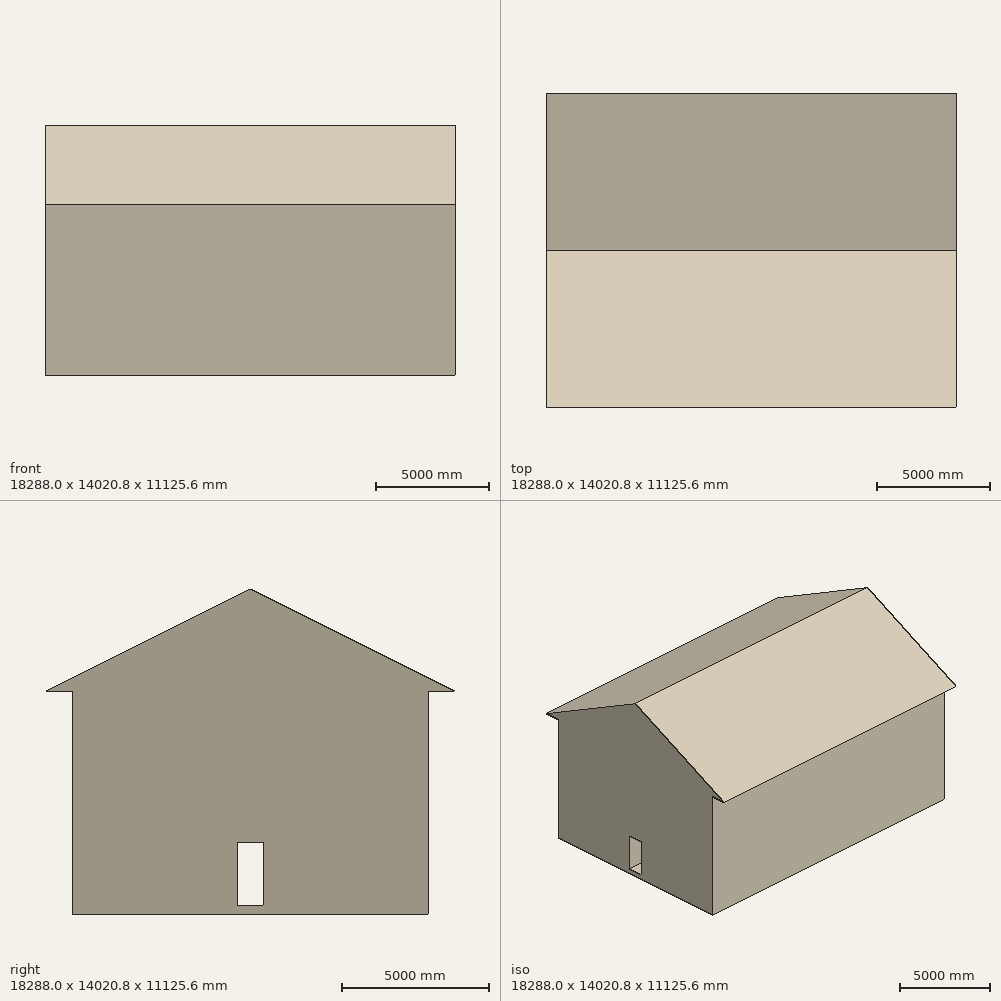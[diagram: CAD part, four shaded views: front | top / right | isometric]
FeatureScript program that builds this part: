
annotation { "Feature Type Name" : "Feature", "Feature Type Description" : "" }
export const myFeature = defineFeature(function(context is Context, id is Id, definition is map)
    precondition{}
    {
        {
            var Q0;
            Q0=qCreatedBy(makeId("Right.planeOp"),FACE);
            var sketch = newSketch(context, id + "F0", { "sketchPlane" : qUnion([Q0])});
            skLineSegment(sketch, "E0", {"start": v(0, 0) * mm, "end": v(-6096, 0) * mm});
            skLineSegment(sketch, "E1", {"start": v(-6096, 0) * mm, "end": v(-12192, 0) * mm});
            skLineSegment(sketch, "E2", {"start": v(-6096, 0) * mm, "end": v(-6096, 3048) * mm});
            skLineSegment(sketch, "E3", {"start": v(-12192, 0) * mm, "end": v(-6096, 3048) * mm});
            skLineSegment(sketch, "E4", {"start": v(0, 0) * mm, "end": v(-6096, 3048) * mm});
            skLineSegment(sketch, "E5", {"start": v(-12192, 0) * mm, "end": v(-12192, -7315.2) * mm});
            skLineSegment(sketch, "E6", {"start": v(-12192, -7315.2) * mm, "end": v(0, -7315.2) * mm});
            skLineSegment(sketch, "E7", {"start": v(0, 0) * mm, "end": v(0, -7315.2) * mm});
            skLineSegment(sketch, "E8", {"start": v(-12192, -7315.2) * mm, "end": v(-12192, -7620) * mm});
            skLineSegment(sketch, "E9", {"start": v(0, -7315.2) * mm, "end": v(0, -7620) * mm});
            skLineSegment(sketch, "E10", {"start": v(-12192, -7620) * mm, "end": v(0, -7620) * mm});
            skLineSegment(sketch, "E11", {"start": v(-6096, -7315.2) * mm, "end": v(-6553.2, -7315.2) * mm});
            skLineSegment(sketch, "E12", {"start": v(-6553.2, -7315.2) * mm, "end": v(-6553.2, -5181.6) * mm});
            skLineSegment(sketch, "E13", {"start": v(-6553.2, -5181.6) * mm, "end": v(-5638.8, -5181.6) * mm});
            skLineSegment(sketch, "E14", {"start": v(-5638.8, -5181.6) * mm, "end": v(-5638.8, -7315.2) * mm});
            skLineSegment(sketch, "E15", {"start": v(0, 0) * mm, "end": v(914.4, 0) * mm});
            skLineSegment(sketch, "E16", {"start": v(-12192, 0) * mm, "end": v(-13106.4, 0) * mm});
            skLineSegment(sketch, "E17", {"start": v(-13106.4, 0) * mm, "end": v(-6095.25, 3505.58) * mm});
            skLineSegment(sketch, "E18", {"start": v(-6095.25, 3505.58) * mm, "end": v(-6096, 3048) * mm});
            skLineSegment(sketch, "E19", {"start": v(-6095.25, 3505.58) * mm, "end": v(914.4, 0) * mm});
            skLineSegment(sketch, "E20.bottom", {"start": v(-10668, -914.4) * mm, "end": v(-9169.03, -914.4) * mm});
            skLineSegment(sketch, "E20.top", {"start": v(-10668, -2354.4) * mm, "end": v(-9169.03, -2354.4) * mm});
            skLineSegment(sketch, "E20.left", {"start": v(-10668, -914.4) * mm, "end": v(-10668, -2354.4) * mm});
            skLineSegment(sketch, "E20.right", {"start": v(-9169.03, -914.4) * mm, "end": v(-9169.03, -2354.4) * mm});
            skLineSegment(sketch, "E21.bottom", {"start": v(-3048, -914.4) * mm, "end": v(-1524, -914.4) * mm});
            skLineSegment(sketch, "E21.top", {"start": v(-3048, -2743.2) * mm, "end": v(-1524, -2743.2) * mm});
            skLineSegment(sketch, "E21.left", {"start": v(-3048, -914.4) * mm, "end": v(-3048, -2743.2) * mm});
            skLineSegment(sketch, "E21.right", {"start": v(-1524, -914.4) * mm, "end": v(-1524, -2743.2) * mm});
            skLineSegment(sketch, "E22.bottom", {"start": v(-10668, -4267.2) * mm, "end": v(-9144, -4267.2) * mm});
            skLineSegment(sketch, "E22.top", {"start": v(-10668, -5791.2) * mm, "end": v(-9144, -5791.2) * mm});
            skLineSegment(sketch, "E22.left", {"start": v(-10668, -4267.2) * mm, "end": v(-10668, -5791.2) * mm});
            skLineSegment(sketch, "E22.right", {"start": v(-9144, -4267.2) * mm, "end": v(-9144, -5791.2) * mm});
            skLineSegment(sketch, "E23.0", {"start": v(-10673, -909.4) * mm, "end": v(-10673, -2359.4) * mm});
            skLineSegment(sketch, "E23.1", {"start": v(-10673, -909.4) * mm, "end": v(-9164.03, -909.4) * mm});
            skLineSegment(sketch, "E23.2", {"start": v(-9164.03, -909.4) * mm, "end": v(-9164.03, -2359.4) * mm});
            skLineSegment(sketch, "E23.3", {"start": v(-10673, -2359.4) * mm, "end": v(-9164.03, -2359.4) * mm});
            skCircle(sketch, "E24.cCircle", {"center": v(-3048, -5791.2) * mm, "radius": 834.28 * mm, "construction": true});
            skLineSegment(sketch, "E24.0", {"start": v(-2270.31, -6097.77) * mm, "end": v(-2314.87, -6192.82) * mm});
            skLineSegment(sketch, "E24.1", {"start": v(-2314.87, -6192.82) * mm, "end": v(-2370.99, -6281.54) * mm});
            skLineSegment(sketch, "E24.2", {"start": v(-2370.99, -6281.54) * mm, "end": v(-2437.78, -6362.53) * mm});
            skLineSegment(sketch, "E24.3", {"start": v(-2437.78, -6362.53) * mm, "end": v(-2514.2, -6434.5) * mm});
            skLineSegment(sketch, "E24.4", {"start": v(-2514.2, -6434.5) * mm, "end": v(-2599.04, -6496.34) * mm});
            skLineSegment(sketch, "E24.5", {"start": v(-2599.04, -6496.34) * mm, "end": v(-2690.95, -6547.04) * mm});
            skLineSegment(sketch, "E24.6", {"start": v(-2690.95, -6547.04) * mm, "end": v(-2788.5, -6585.83) * mm});
            skLineSegment(sketch, "E24.7", {"start": v(-2788.5, -6585.83) * mm, "end": v(-2890.14, -6612.1) * mm});
            skLineSegment(sketch, "E24.8", {"start": v(-2890.14, -6612.1) * mm, "end": v(-2994.27, -6625.4) * mm});
            skLineSegment(sketch, "E24.9", {"start": v(-2994.27, -6625.4) * mm, "end": v(-3099.25, -6625.56) * mm});
            skLineSegment(sketch, "E24.10", {"start": v(-3099.25, -6625.56) * mm, "end": v(-3203.42, -6612.56) * mm});
            skLineSegment(sketch, "E24.11", {"start": v(-3203.42, -6612.56) * mm, "end": v(-3305.14, -6586.6) * mm});
            skLineSegment(sketch, "E24.12", {"start": v(-3305.14, -6586.6) * mm, "end": v(-3402.8, -6548.1) * mm});
            skLineSegment(sketch, "E24.13", {"start": v(-3402.8, -6548.1) * mm, "end": v(-3494.87, -6497.67) * mm});
            skLineSegment(sketch, "E24.14", {"start": v(-3494.87, -6497.67) * mm, "end": v(-3579.89, -6436.09) * mm});
            skLineSegment(sketch, "E24.15", {"start": v(-3579.89, -6436.09) * mm, "end": v(-3656.52, -6364.34) * mm});
            skLineSegment(sketch, "E24.16", {"start": v(-3656.52, -6364.34) * mm, "end": v(-3723.55, -6283.55) * mm});
            skLineSegment(sketch, "E24.17", {"start": v(-3723.55, -6283.55) * mm, "end": v(-3779.93, -6195) * mm});
            skLineSegment(sketch, "E24.18", {"start": v(-3779.93, -6195) * mm, "end": v(-3824.77, -6100.08) * mm});
            skLineSegment(sketch, "E24.19", {"start": v(-3824.77, -6100.08) * mm, "end": v(-3857.36, -6000.3) * mm});
            skLineSegment(sketch, "E24.20", {"start": v(-3857.36, -6000.3) * mm, "end": v(-3877.18, -5897.2) * mm});
            skLineSegment(sketch, "E24.21", {"start": v(-3877.18, -5897.2) * mm, "end": v(-3883.93, -5792.44) * mm});
            skLineSegment(sketch, "E24.22", {"start": v(-3883.93, -5792.44) * mm, "end": v(-3877.5, -5687.66) * mm});
            skLineSegment(sketch, "E24.23", {"start": v(-3877.5, -5687.66) * mm, "end": v(-3857.98, -5584.52) * mm});
            skLineSegment(sketch, "E24.24", {"start": v(-3857.98, -5584.52) * mm, "end": v(-3825.69, -5484.63) * mm});
            skLineSegment(sketch, "E24.25", {"start": v(-3825.69, -5484.63) * mm, "end": v(-3781.13, -5389.58) * mm});
            skLineSegment(sketch, "E24.26", {"start": v(-3781.13, -5389.58) * mm, "end": v(-3725.01, -5300.86) * mm});
            skLineSegment(sketch, "E24.27", {"start": v(-3725.01, -5300.86) * mm, "end": v(-3658.22, -5219.87) * mm});
            skLineSegment(sketch, "E24.28", {"start": v(-3658.22, -5219.87) * mm, "end": v(-3581.8, -5147.9) * mm});
            skLineSegment(sketch, "E24.29", {"start": v(-3581.8, -5147.9) * mm, "end": v(-3496.96, -5086.06) * mm});
            skLineSegment(sketch, "E24.30", {"start": v(-3496.96, -5086.06) * mm, "end": v(-3405.05, -5035.36) * mm});
            skLineSegment(sketch, "E24.31", {"start": v(-3405.05, -5035.36) * mm, "end": v(-3307.5, -4996.57) * mm});
            skLineSegment(sketch, "E24.32", {"start": v(-3307.5, -4996.57) * mm, "end": v(-3205.86, -4970.3) * mm});
            skLineSegment(sketch, "E24.33", {"start": v(-3205.86, -4970.3) * mm, "end": v(-3101.73, -4957) * mm});
            skLineSegment(sketch, "E24.34", {"start": v(-3101.73, -4957) * mm, "end": v(-2996.75, -4956.84) * mm});
            skLineSegment(sketch, "E24.35", {"start": v(-2996.75, -4956.84) * mm, "end": v(-2892.58, -4969.84) * mm});
            skLineSegment(sketch, "E24.36", {"start": v(-2892.58, -4969.84) * mm, "end": v(-2790.86, -4995.8) * mm});
            skLineSegment(sketch, "E24.37", {"start": v(-2790.86, -4995.8) * mm, "end": v(-2693.2, -5034.3) * mm});
            skLineSegment(sketch, "E24.38", {"start": v(-2693.2, -5034.3) * mm, "end": v(-2601.13, -5084.73) * mm});
            skLineSegment(sketch, "E24.39", {"start": v(-2601.13, -5084.73) * mm, "end": v(-2516.11, -5146.31) * mm});
            skLineSegment(sketch, "E24.40", {"start": v(-2516.11, -5146.31) * mm, "end": v(-2439.48, -5218.06) * mm});
            skLineSegment(sketch, "E24.41", {"start": v(-2439.48, -5218.06) * mm, "end": v(-2372.45, -5298.85) * mm});
            skLineSegment(sketch, "E24.42", {"start": v(-2372.45, -5298.85) * mm, "end": v(-2316.07, -5387.4) * mm});
            skLineSegment(sketch, "E24.43", {"start": v(-2316.07, -5387.4) * mm, "end": v(-2271.23, -5482.32) * mm});
            skLineSegment(sketch, "E24.44", {"start": v(-2271.23, -5482.32) * mm, "end": v(-2238.64, -5582.1) * mm});
            skLineSegment(sketch, "E24.45", {"start": v(-2238.64, -5582.1) * mm, "end": v(-2218.82, -5685.2) * mm});
            skLineSegment(sketch, "E24.46", {"start": v(-2218.82, -5685.2) * mm, "end": v(-2212.07, -5789.96) * mm});
            skLineSegment(sketch, "E24.47", {"start": v(-2212.07, -5789.96) * mm, "end": v(-2218.5, -5894.74) * mm});
            skLineSegment(sketch, "E24.48", {"start": v(-2218.5, -5894.74) * mm, "end": v(-2238.02, -5997.88) * mm});
            skLineSegment(sketch, "E24.49", {"start": v(-2238.02, -5997.88) * mm, "end": v(-2270.31, -6097.77) * mm});
            skPoint(sketch, "E24.0.midPoint", {"position": v(-2292.6, -6145.3) * mm});
            skSolve(sketch);
        }
        {
            var Q0;
            Q0=makeQuery(id+"F0.imprint","IMPRINT",FACE,{"disambiguationData":[TD([[makeQuery(id+"F0.imprint","IMPRINT",EDGE,{"derivedFrom":sQuery(id+"F0.wireOp",EDGE,"E4")}),-1.0]])]});
            var Q1;
            Q1=makeQuery(id+"F0.imprint","IMPRINT",FACE,{"disambiguationData":[TD([[makeQuery(id+"F0.imprint","IMPRINT",EDGE,{"derivedFrom":sQuery(id+"F0.wireOp",EDGE,"E1")}),-1.0]])]});
            var Q2;
            Q2=makeQuery(id+"F0.imprint","IMPRINT",FACE,{"disambiguationData":[TD([[makeQuery(id+"F0.imprint","IMPRINT",EDGE,{"derivedFrom":sQuery(id+"F0.wireOp",EDGE,"E0")}),1.0]])]});
            var Q3;
            Q3=makeQuery(id+"F0.imprint","IMPRINT",FACE,{"disambiguationData":[TD([[makeQuery(id+"F0.imprint","IMPRINT",EDGE,{"derivedFrom":sQuery(id+"F0.wireOp",EDGE,"E21.bottom")}),-1.0]])]});
            var Q4;
            Q4=makeQuery(id+"F0.imprint","IMPRINT",FACE,{"disambiguationData":[TD([[makeQuery(id+"F0.imprint","IMPRINT",EDGE,{"derivedFrom":sQuery(id+"F0.wireOp",EDGE,"E22.bottom")}),-1.0]])]});
            var Q5;
            Q5=makeQuery(id+"F0.imprint","IMPRINT",FACE,{"disambiguationData":[TD([[makeQuery(id+"F0.imprint","IMPRINT",EDGE,{"derivedFrom":sQuery(id+"F0.wireOp",EDGE,"E24.0")}),-1.0]])]});
            var Q6;
            Q6=makeQuery(id+"F0.imprint","IMPRINT",FACE,{"disambiguationData":[TD([[makeQuery(id+"F0.imprint","IMPRINT",EDGE,{"derivedFrom":sQuery(id+"F0.wireOp",EDGE,"E3")}),1.0]])]});
            var Q7;
            {var subQ0=sQuery(id+"F0.wireOp",EDGE,"E8");Q7=makeQuery(id+"F0.imprint","IMPRINT",FACE,{"disambiguationData":[TD([[makeQuery(id+"F0.imprint","IMPRINT",EDGE,{"derivedFrom":subQ0}),1.0]])]});}
            var Q8;
            {var subQ0=sQuery(id+"F0.wireOp",EDGE,"E11");Q8=makeQuery(id+"F0.imprint","IMPRINT",FACE,{"disambiguationData":[TD([[makeQuery(id+"F0.imprint","IMPRINT",EDGE,{"derivedFrom":subQ0}),-1.0]])]});}
            var Q9;
            Q9=makeQuery(id+"F0.imprint","IMPRINT",FACE,{"disambiguationData":[TD([[makeQuery(id+"F0.imprint","IMPRINT",EDGE,{"derivedFrom":sQuery(id+"F0.wireOp",EDGE,"E0")}),-1.0]])]});
            var Q10;
            Q10=makeQuery(id+"F0.imprint","IMPRINT",FACE,{"disambiguationData":[TD([[makeQuery(id+"F0.imprint","IMPRINT",EDGE,{"derivedFrom":sQuery(id+"F0.wireOp",EDGE,"E20.bottom")}),-1.0]])]});
            var Q11;
            Q11=makeQuery(id+"F0.imprint","IMPRINT",FACE,{"disambiguationData":[TD([[makeQuery(id+"F0.imprint","IMPRINT",EDGE,{"derivedFrom":sQuery(id+"F0.wireOp",EDGE,"E20.bottom")}),1.0]])]});
            extrude(context, id + "F1", {"entities" : qUnion([Q0, Q1, Q2, Q3, Q4, Q5, Q6, Q7, Q8, Q9, Q10, Q11]), "depth" : 18288 * mm, "offsetDistance" : 30.48 * mm});
        }
    });
